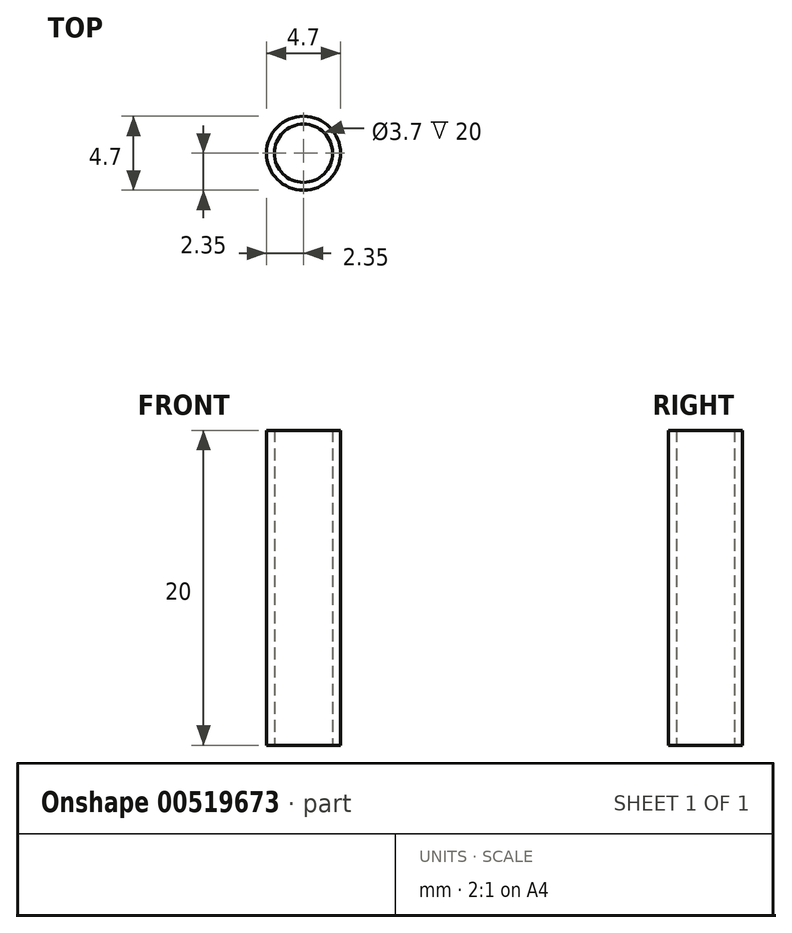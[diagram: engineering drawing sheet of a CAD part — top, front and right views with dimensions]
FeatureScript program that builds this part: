
annotation { "Feature Type Name" : "Feature", "Feature Type Description" : "" }
export const myFeature = defineFeature(function(context is Context, id is Id, definition is map)
    precondition{}
    {
        {
            var Q0;
            Q0=qCreatedBy(makeId("Top.planeOp"),FACE);
            var sketch = newSketch(context, id + "F0", { "sketchPlane" : qUnion([Q0])});
            skCircle(sketch, "E0", {"center": v(0, 0) * mm, "radius": 1.85 * mm});
            skCircle(sketch, "E1", {"center": v(0, 0) * mm, "radius": 2.35 * mm});
            skSolve(sketch);
        }
        {
            var Q0;
            Q0=makeQuery(id+"F0.imprint","IMPRINT",FACE,{"disambiguationData":[TD([[makeQuery(id+"F0.imprint","IMPRINT",EDGE,{"derivedFrom":sQuery(id+"F0.wireOp",EDGE,"E0")}),-1.0]])]});
            extrude(context, id + "F1", {"entities" : qUnion([Q0]), "depth" : 20 * mm, "offsetDistance" : 25 * mm});
        }
    });
